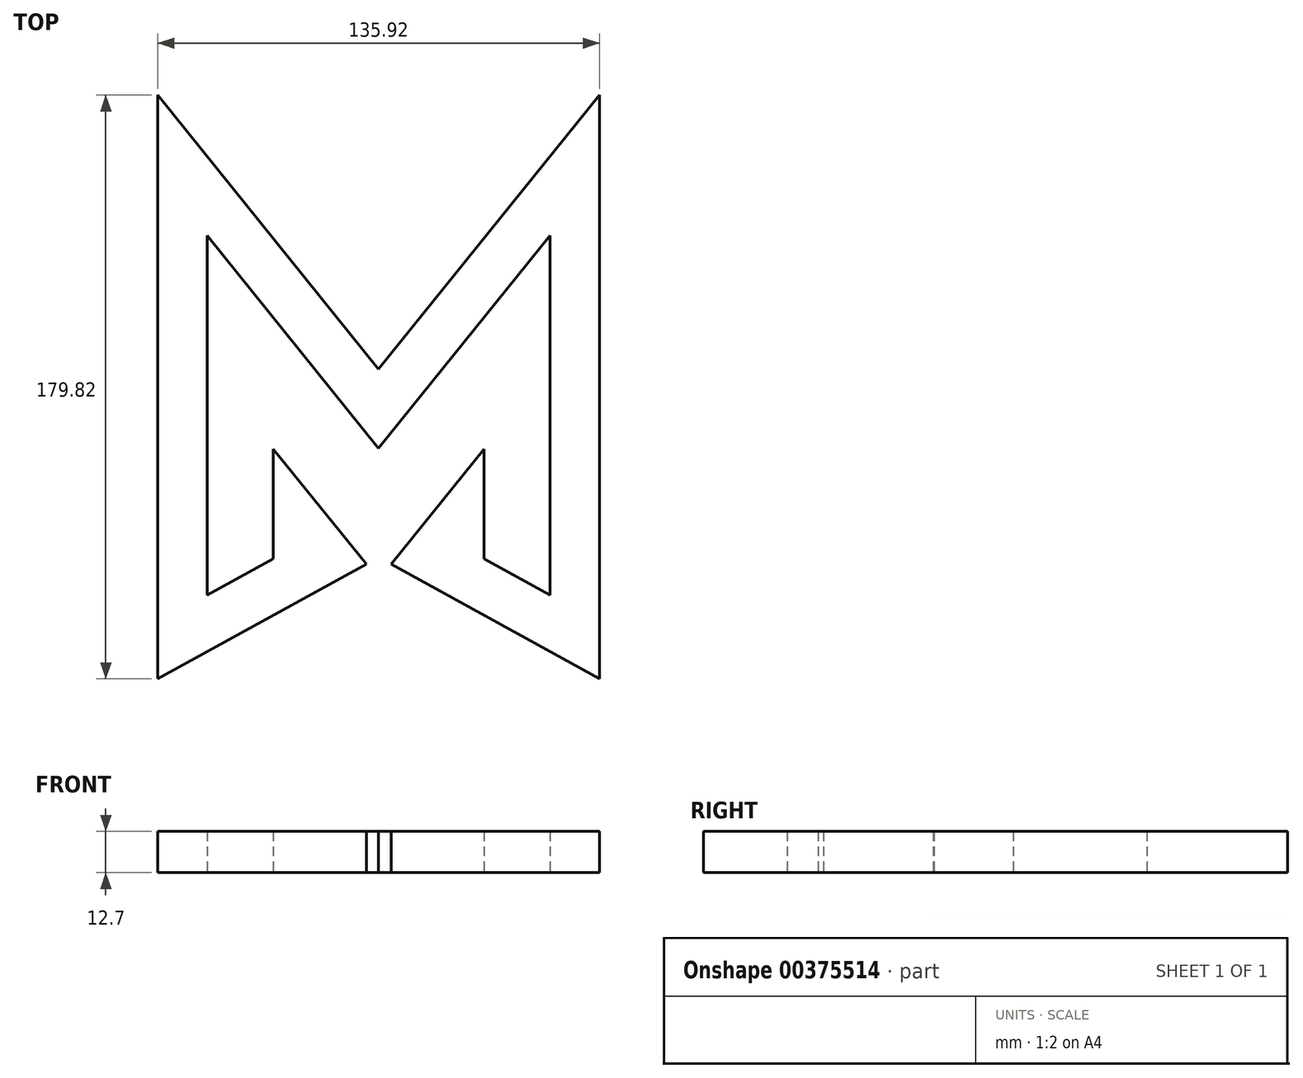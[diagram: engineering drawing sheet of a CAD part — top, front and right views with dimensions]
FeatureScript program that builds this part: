
annotation { "Feature Type Name" : "Feature", "Feature Type Description" : "" }
export const myFeature = defineFeature(function(context is Context, id is Id, definition is map)
    precondition{}
    {
        {
            var Q0;
            Q0=qCreatedBy(makeId("Top.planeOp"),FACE);
            var sketch = newSketch(context, id + "F0", { "sketchPlane" : qUnion([Q0])});
            skLineSegment(sketch, "E0", {"start": v(-32.4, -34.12) * mm, "end": v(-52.72, -45.3) * mm});
            skLineSegment(sketch, "E1", {"start": v(-52.72, 65.5) * mm, "end": v(-52.72, -45.3) * mm});
            skLineSegment(sketch, "E2", {"start": v(0, 0) * mm, "end": v(-52.72, 65.5) * mm});
            skLineSegment(sketch, "E3", {"start": v(-3.8, -35.77) * mm, "end": v(-32.4, -0.25) * mm});
            skLineSegment(sketch, "E4", {"start": v(-32.4, -0.25) * mm, "end": v(-32.4, -34.12) * mm});
            skLineSegment(sketch, "E5", {"start": v(-67.96, -71.1) * mm, "end": v(-67.96, 108.73) * mm});
            skLineSegment(sketch, "E6", {"start": v(-67.96, 108.73) * mm, "end": v(0, 24.3) * mm});
            skLineSegment(sketch, "E7", {"start": v(-67.96, -71.1) * mm, "end": v(-3.8, -35.77) * mm});
            skLineSegment(sketch, "E8.MirrorCS", {"start": v(67.96, 108.73) * mm, "end": v(0, 24.3) * mm});
            skLineSegment(sketch, "E9.MirrorCS", {"start": v(52.72, 65.5) * mm, "end": v(52.72, -45.3) * mm});
            skLineSegment(sketch, "E10.MirrorCS", {"start": v(67.96, -71.1) * mm, "end": v(3.8, -35.77) * mm});
            skLineSegment(sketch, "E11.MirrorCS", {"start": v(67.96, -71.1) * mm, "end": v(67.96, 108.73) * mm});
            skLineSegment(sketch, "E12.MirrorCS", {"start": v(3.8, -35.77) * mm, "end": v(32.4, -0.25) * mm});
            skLineSegment(sketch, "E13.MirrorCS", {"start": v(32.4, -0.25) * mm, "end": v(32.4, -34.12) * mm});
            skLineSegment(sketch, "E14.MirrorCS", {"start": v(32.4, -34.12) * mm, "end": v(52.72, -45.3) * mm});
            skLineSegment(sketch, "E15.MirrorCS", {"start": v(0, 0) * mm, "end": v(52.72, 65.5) * mm});
            skSolve(sketch);
        }
        {
            var Q0;
            Q0=makeQuery(id+"F0.imprint","IMPRINT",FACE,{"disambiguationData":[TD([[makeQuery(id+"F0.imprint","IMPRINT",EDGE,{"derivedFrom":sQuery(id+"F0.wireOp",EDGE,"E0")}),1.0]])]});
            extrude(context, id + "F1", {"entities" : qUnion([Q0]), "depth" : 12.7 * mm});
        }
    });
